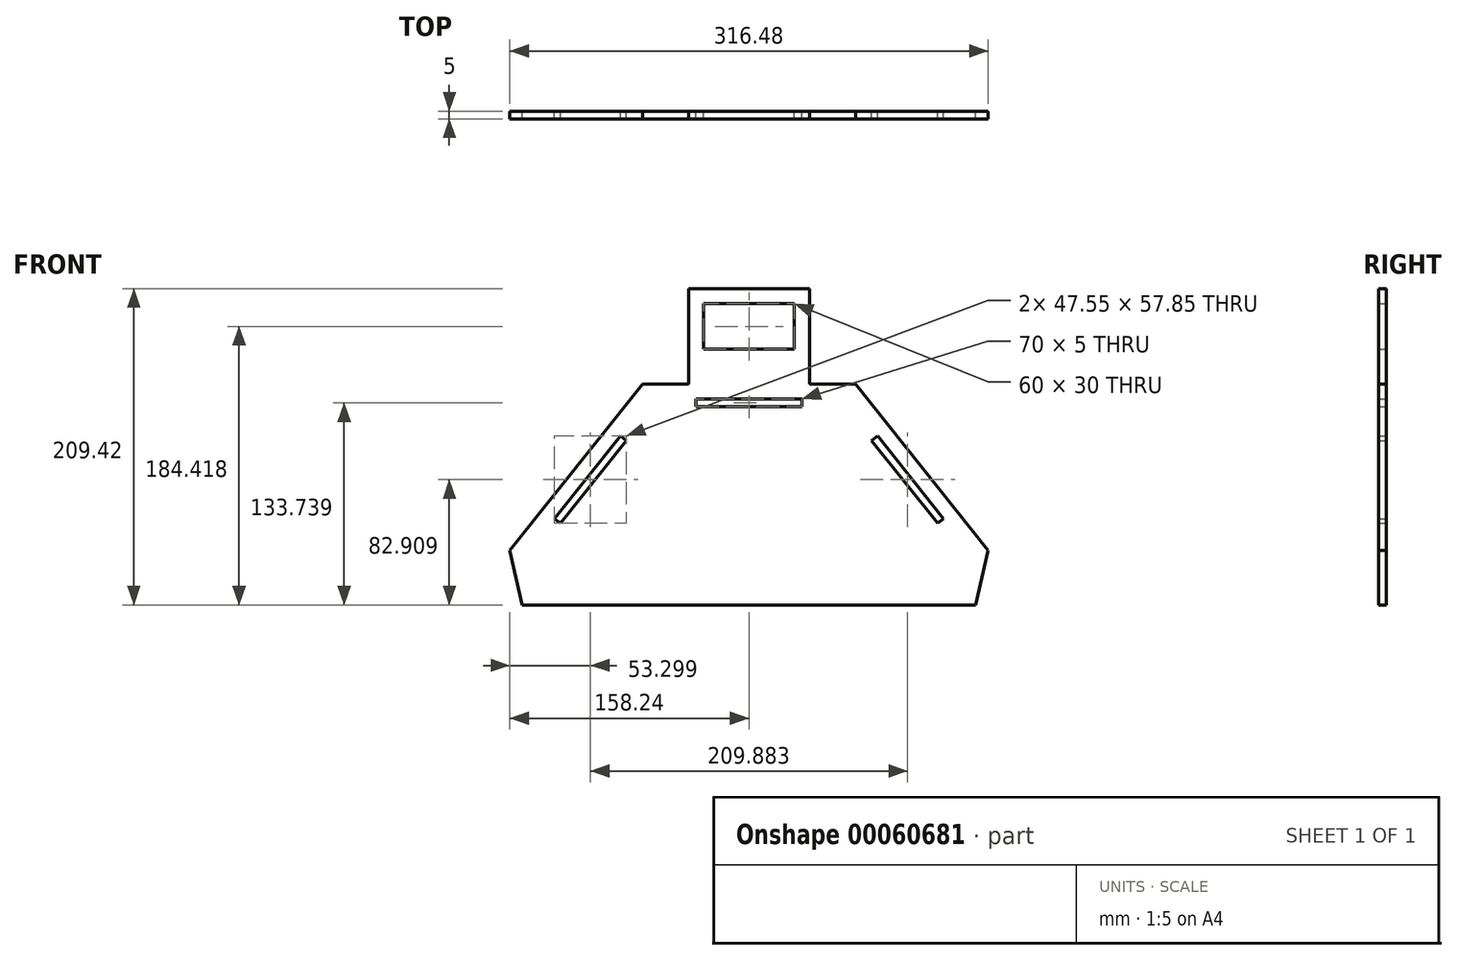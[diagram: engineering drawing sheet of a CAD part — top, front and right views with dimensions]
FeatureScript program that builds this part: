
annotation { "Feature Type Name" : "Feature", "Feature Type Description" : "" }
export const myFeature = defineFeature(function(context is Context, id is Id, definition is map)
    precondition{}
    {
        {
            var Q0;
            Q0=qCreatedBy(makeId("Front.planeOp"),FACE);
            var sketch = newSketch(context, id + "F0", { "sketchPlane" : qUnion([Q0])});
            skLineSegment(sketch, "E0.0", {"start": v(-70.43, 146.24) * mm, "end": v(-40, 146.24) * mm});
            skLineSegment(sketch, "E0.1", {"start": v(70.43, 146.24) * mm, "end": v(158.24, 36.12) * mm});
            skLineSegment(sketch, "E0.2", {"start": v(158.24, 36.12) * mm, "end": v(150, 0) * mm});
            skLineSegment(sketch, "E0.5", {"start": v(-150, 0) * mm, "end": v(-158.24, 36.12) * mm});
            skLineSegment(sketch, "E0.6", {"start": v(-158.24, 36.12) * mm, "end": v(-70.43, 146.24) * mm});
            skPoint(sketch, "E0.0.midPoint", {"position": v(0, 146.24) * mm});
            skLineSegment(sketch, "E1", {"start": v(-150, 0) * mm, "end": v(150, 0) * mm});
            skPoint(sketch, "E2.orphan", {"position": v(-126.9, -101.2) * mm});
            skLineSegment(sketch, "E3.0", {"start": v(-147.42, 33.65) * mm, "end": v(-65.6, 136.24) * mm, "construction": true});
            skLineSegment(sketch, "E3.1", {"start": v(65.6, 136.24) * mm, "end": v(147.42, 33.65) * mm, "construction": true});
            skLineSegment(sketch, "E3.2", {"start": v(147.42, 33.65) * mm, "end": v(142.03, 10) * mm, "construction": true});
            skLineSegment(sketch, "E3.3", {"start": v(-65.6, 136.24) * mm, "end": v(65.6, 136.24) * mm, "construction": true});
            skLineSegment(sketch, "E3.4", {"start": v(-142.03, 10) * mm, "end": v(142.03, 10) * mm, "construction": true});
            skLineSegment(sketch, "E3.5", {"start": v(-142.03, 10) * mm, "end": v(-147.42, 33.65) * mm, "construction": true});
            skLineSegment(sketch, "E4.bottom", {"start": v(-35, 136.24) * mm, "end": v(35, 136.24) * mm});
            skLineSegment(sketch, "E4.top", {"start": v(-35, 131.24) * mm, "end": v(35, 131.24) * mm});
            skLineSegment(sketch, "E4.left", {"start": v(-35, 136.24) * mm, "end": v(-35, 131.24) * mm});
            skLineSegment(sketch, "E4.right", {"start": v(35, 136.24) * mm, "end": v(35, 131.24) * mm});
            skLineSegment(sketch, "E5", {"start": v(0, 131.24) * mm, "end": v(0, 136.24) * mm, "construction": true});
            skLineSegment(sketch, "E6", {"start": v(-124.8, 53.99) * mm, "end": v(-81.16, 108.71) * mm});
            skLineSegment(sketch, "E7", {"start": v(-81.16, 108.71) * mm, "end": v(-85.07, 111.83) * mm});
            skLineSegment(sketch, "E8", {"start": v(-124.8, 53.99) * mm, "end": v(-128.72, 57.1) * mm});
            skLineSegment(sketch, "E9", {"start": v(-85.07, 111.83) * mm, "end": v(-128.72, 57.1) * mm});
            skLineSegment(sketch, "E10", {"start": v(0, 146.24) * mm, "end": v(0, 0) * mm, "construction": true});
            skLineSegment(sketch, "E11.MirrorCS", {"start": v(124.8, 53.99) * mm, "end": v(81.16, 108.71) * mm});
            skLineSegment(sketch, "E12.MirrorCS", {"start": v(81.16, 108.71) * mm, "end": v(85.07, 111.83) * mm});
            skLineSegment(sketch, "E13.MirrorCS", {"start": v(85.07, 111.83) * mm, "end": v(128.72, 57.1) * mm});
            skLineSegment(sketch, "E14.MirrorCS", {"start": v(124.8, 53.99) * mm, "end": v(128.72, 57.1) * mm});
            skLineSegment(sketch, "E15.top", {"start": v(0, 199.42) * mm, "end": v(30, 199.42) * mm});
            skLineSegment(sketch, "E15.left", {"start": v(0, 169.42) * mm, "end": v(0, 199.42) * mm, "construction": true});
            skLineSegment(sketch, "E15.right", {"start": v(30, 169.42) * mm, "end": v(30, 199.42) * mm});
            skLineSegment(sketch, "E16.MirrorCS", {"start": v(-30, 169.42) * mm, "end": v(-30, 199.42) * mm});
            skLineSegment(sketch, "E17.MirrorCS", {"start": v(0, 199.42) * mm, "end": v(-30, 199.42) * mm});
            skLineSegment(sketch, "E18.0", {"start": v(-40, 146.24) * mm, "end": v(-40, 209.42) * mm});
            skLineSegment(sketch, "E18.1", {"start": v(1.5, 209.42) * mm, "end": v(-40, 209.42) * mm});
            skLineSegment(sketch, "E18.2", {"start": v(1.5, 209.42) * mm, "end": v(40, 209.42) * mm});
            skLineSegment(sketch, "E18.3", {"start": v(40, 146.24) * mm, "end": v(40, 209.42) * mm});
            skLineSegment(sketch, "E19", {"start": v(30, 169.42) * mm, "end": v(-30, 169.42) * mm});
            skPoint(sketch, "E20.orphan", {"position": v(-30, 146.24) * mm});
            skLineSegment(sketch, "E21.trimOffspring", {"start": v(40, 146.24) * mm, "end": v(70.43, 146.24) * mm});
            skPoint(sketch, "E22.orphan", {"position": v(30, 146.24) * mm});
            skSolve(sketch);
        }
        {
            var Q0;
            Q0=makeQuery(id+"F0.imprint","IMPRINT",FACE,{"disambiguationData":[TD([[makeQuery(id+"F0.imprint","IMPRINT",EDGE,{"derivedFrom":sQuery(id+"F0.wireOp",EDGE,"E0.0")}),-1.0]])]});
            extrude(context, id + "F1", {"entities" : qUnion([Q0]), "depth" : 5 * mm});
        }
    });
